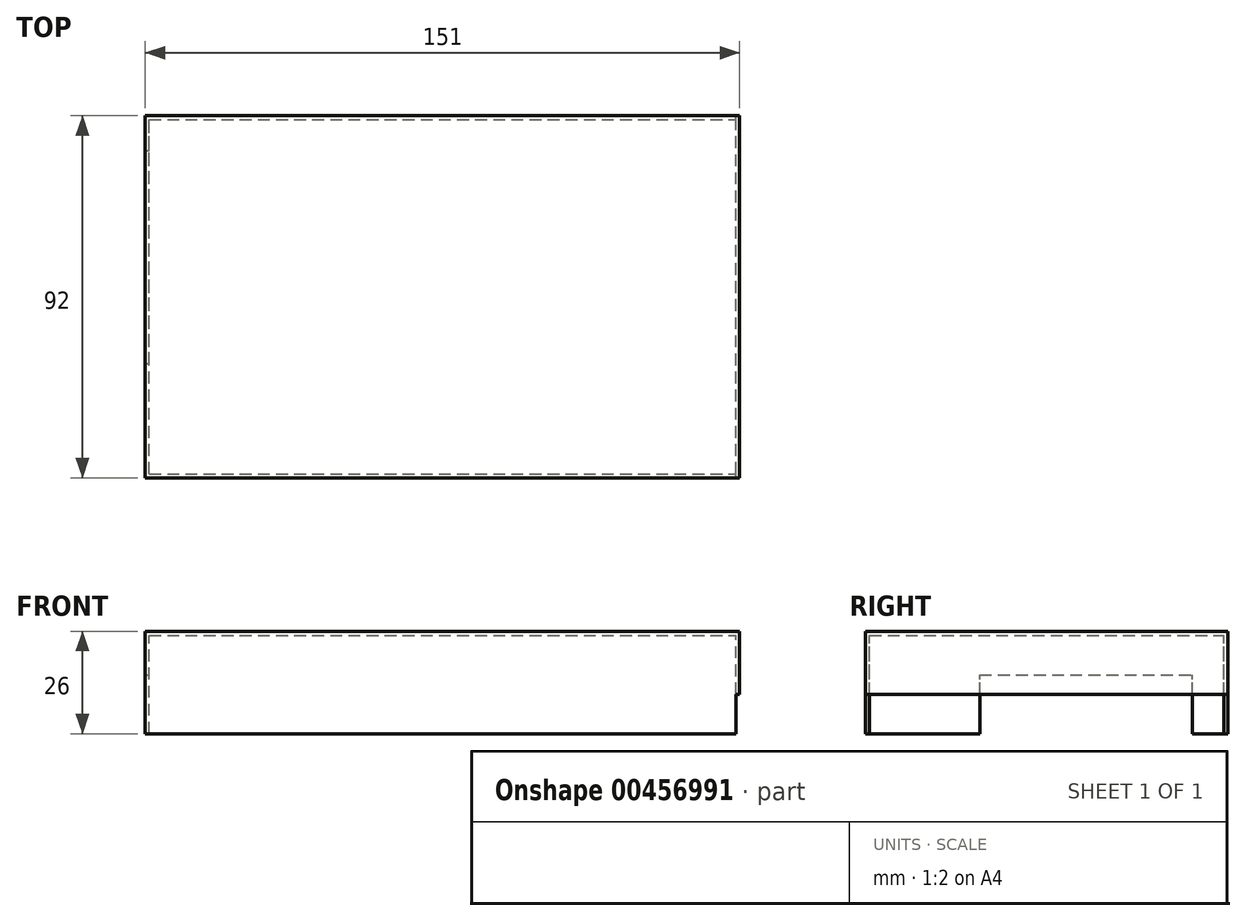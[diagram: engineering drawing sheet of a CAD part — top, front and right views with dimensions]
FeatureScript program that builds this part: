
annotation { "Feature Type Name" : "Feature", "Feature Type Description" : "" }
export const myFeature = defineFeature(function(context is Context, id is Id, definition is map)
    precondition{}
    {
        {
            var Q0;
            Q0=qCreatedBy(makeId("Top.planeOp"),FACE);
            var sketch = newSketch(context, id + "F0", { "sketchPlane" : qUnion([Q0])});
            skLineSegment(sketch, "E0.bottom", {"start": v(0, 0) * mm, "end": v(151, 0) * mm});
            skLineSegment(sketch, "E0.top", {"start": v(0, 92) * mm, "end": v(151, 92) * mm});
            skLineSegment(sketch, "E0.left", {"start": v(0, 0) * mm, "end": v(0, 92) * mm});
            skLineSegment(sketch, "E0.right", {"start": v(151, 0) * mm, "end": v(151, 92) * mm});
            skLineSegment(sketch, "E1.0", {"start": v(1, 1) * mm, "end": v(150, 1) * mm});
            skLineSegment(sketch, "E1.1", {"start": v(1, 1) * mm, "end": v(1, 91) * mm});
            skLineSegment(sketch, "E1.2", {"start": v(1, 91) * mm, "end": v(150, 91) * mm});
            skLineSegment(sketch, "E1.3", {"start": v(150, 1) * mm, "end": v(150, 91) * mm});
            skLineSegment(sketch, "E2", {"start": v(150, 91) * mm, "end": v(150, 92) * mm});
            skLineSegment(sketch, "E3", {"start": v(150, 1) * mm, "end": v(150, 0) * mm});
            skLineSegment(sketch, "E4", {"start": v(0, 29) * mm, "end": v(1, 29) * mm});
            skLineSegment(sketch, "E5", {"start": v(1, 83) * mm, "end": v(0, 83) * mm});
            skSolve(sketch);
        }
        {
            var Q0;
            {var subQ0=sQuery(id+"F0.wireOp",EDGE,"E0.left");Q0=makeQuery(id+"F0.imprint","IMPRINT",FACE,{"disambiguationData":[TD([[makeQuery(id+"F0.imprint","IMPRINT",EDGE,{"derivedFrom":subQ0}),-1.0]])]});}
            var Q1;
            {var subQ0=sQuery(id+"F0.wireOp",EDGE,"E0.right");Q1=makeQuery(id+"F0.imprint","IMPRINT",FACE,{"disambiguationData":[TD([[makeQuery(id+"F0.imprint","IMPRINT",EDGE,{"derivedFrom":subQ0}),1.0]])]});}
            var Q2;
            Q2=makeQuery(id+"F0.imprint","IMPRINT",FACE,{"disambiguationData":[TD([[makeQuery(id+"F0.imprint","IMPRINT",EDGE,{"derivedFrom":sQuery(id+"F0.wireOp",EDGE,"E1.0")}),1.0]])]});
            var Q3;
            {var subQ0=sQuery(id+"F0.wireOp",EDGE,"E1.2");Q3=makeQuery(id+"F0.imprint","IMPRINT",FACE,{"disambiguationData":[TD([[makeQuery(id+"F0.imprint","IMPRINT",EDGE,{"derivedFrom":subQ0}),1.0]])]});}
            var Q4;
            {var subQ0=sQuery(id+"F0.wireOp",EDGE,"E1.0");Q4=makeQuery(id+"F0.imprint","IMPRINT",FACE,{"disambiguationData":[TD([[makeQuery(id+"F0.imprint","IMPRINT",EDGE,{"derivedFrom":subQ0}),-1.0]])]});}
            extrude(context, id + "F1", {"entities" : qUnion([Q0, Q1, Q2, Q3, Q4]), "depth" : 1 * mm, "offsetDistance" : 25 * mm});
        }
        {
            var Q0;
            {var subQ0=sQuery(id+"F0.wireOp",EDGE,"E1.0");Q0=makeQuery(id+"F0.imprint","IMPRINT",FACE,{"disambiguationData":[TD([[makeQuery(id+"F0.imprint","IMPRINT",EDGE,{"derivedFrom":subQ0}),-1.0]])]});}
            var Q1;
            {var subQ0=sQuery(id+"F0.wireOp",EDGE,"E1.2");Q1=makeQuery(id+"F0.imprint","IMPRINT",FACE,{"disambiguationData":[TD([[makeQuery(id+"F0.imprint","IMPRINT",EDGE,{"derivedFrom":subQ0}),1.0]])]});}
            extrude(context, id + "F2", {"entities" : qUnion([Q0, Q1]), "operationType" : NewBodyOperationType.ADD, "oppositeDirection" : true, "depth" : 25 * mm, "offsetDistance" : 25 * mm});
        }
        {
            var Q0;
            {var subQ0=sQuery(id+"F0.wireOp",EDGE,"E4");Q0=makeQuery(id+"F0.imprint","IMPRINT",FACE,{"disambiguationData":[TD([[makeQuery(id+"F0.imprint","IMPRINT",EDGE,{"derivedFrom":subQ0}),1.0]])]});}
            extrude(context, id + "F3", {"entities" : qUnion([Q0]), "operationType" : NewBodyOperationType.ADD, "oppositeDirection" : true, "depth" : 10 * mm, "offsetDistance" : 25 * mm});
        }
        {
            var Q0;
            {var subQ0=sQuery(id+"F0.wireOp",EDGE,"E0.right");Q0=makeQuery(id+"F0.imprint","IMPRINT",FACE,{"disambiguationData":[TD([[makeQuery(id+"F0.imprint","IMPRINT",EDGE,{"derivedFrom":subQ0}),1.0]])]});}
            extrude(context, id + "F4", {"entities" : qUnion([Q0]), "operationType" : NewBodyOperationType.ADD, "oppositeDirection" : true, "depth" : 15 * mm, "offsetDistance" : 25 * mm});
        }
    });
